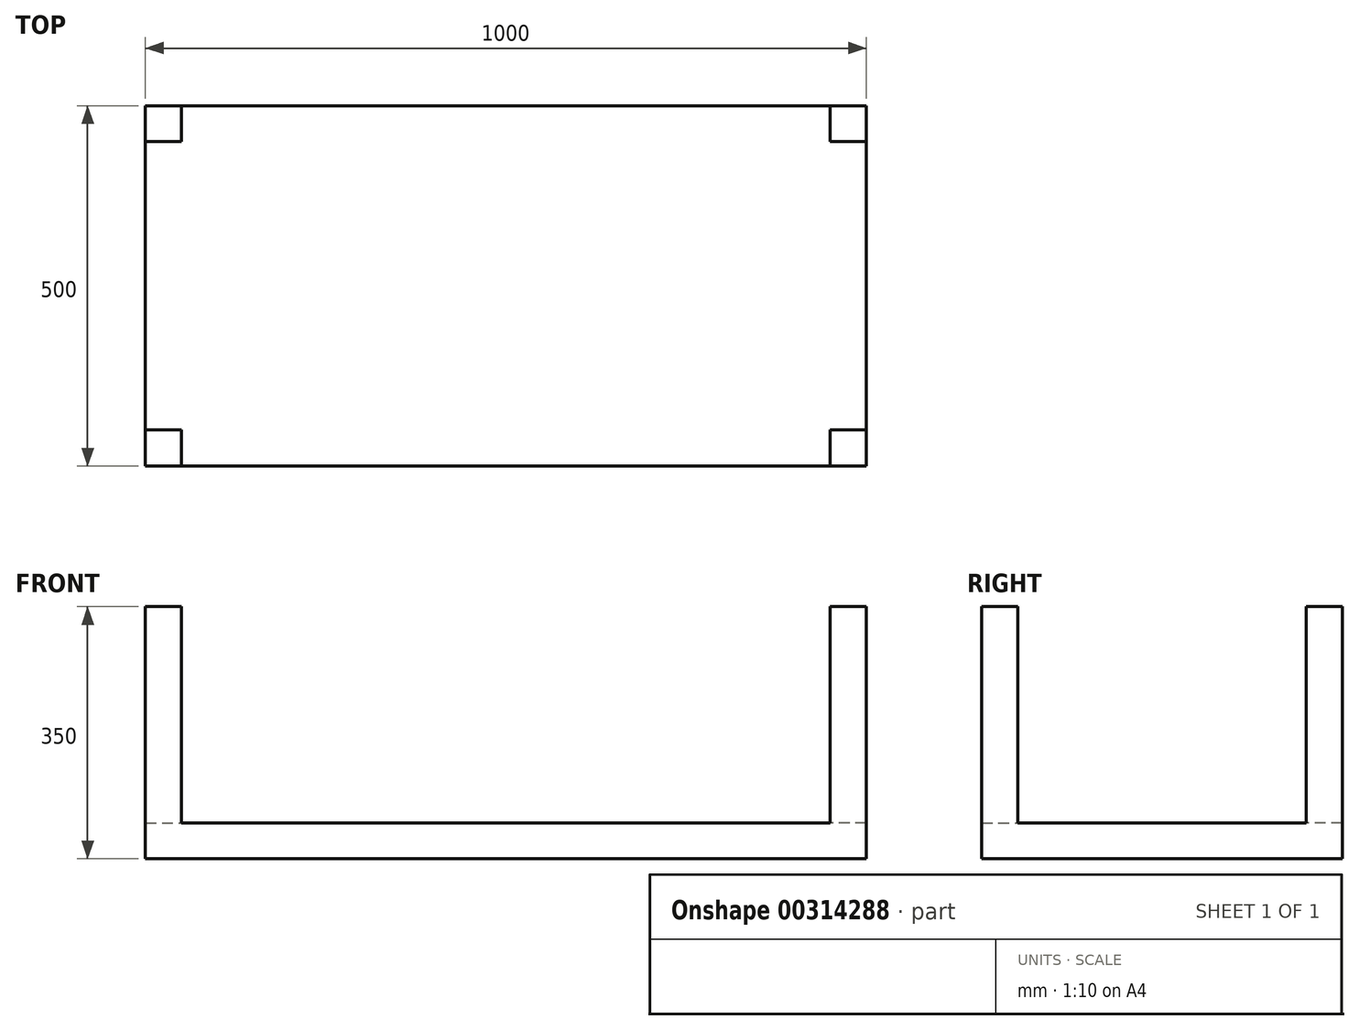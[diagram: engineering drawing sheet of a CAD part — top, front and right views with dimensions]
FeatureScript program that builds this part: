
annotation { "Feature Type Name" : "Feature", "Feature Type Description" : "" }
export const myFeature = defineFeature(function(context is Context, id is Id, definition is map)
    precondition{}
    {
        {
            var Q0;
            Q0=qCreatedBy(makeId("Top.planeOp"),FACE);
            var sketch = newSketch(context, id + "F0", { "sketchPlane" : qUnion([Q0])});
            skLineSegment(sketch, "E0.bottom", {"start": v(-382.04, 267.62) * mm, "end": v(617.96, 267.62) * mm});
            skLineSegment(sketch, "E0.top", {"start": v(-382.04, -232.38) * mm, "end": v(617.96, -232.38) * mm});
            skLineSegment(sketch, "E0.left", {"start": v(-382.04, 267.62) * mm, "end": v(-382.04, -232.38) * mm});
            skLineSegment(sketch, "E0.right", {"start": v(617.96, 267.62) * mm, "end": v(617.96, -232.38) * mm});
            skSolve(sketch);
        }
        {
            var Q0;
            Q0 = qSketchRegion(id + "F0", true);
            extrude(context, id + "F1", {"entities" : qUnion([Q0]), "depth" : 50 * mm});
        }
        {
            var Q0;
            Q0=makeQuery(id+"F1.opExtrude","CAP_FACE",FACE,{"disambiguationData":[OSD([sQuery(id+"F0.wireOp",EDGE,"E0.bottom"),sQuery(id+"F0.wireOp",EDGE,"E0.top"),sQuery(id+"F0.wireOp",EDGE,"E0.left"),sQuery(id+"F0.wireOp",EDGE,"E0.right")])],"isStart":false});
            var sketch = newSketch(context, id + "F2", { "sketchPlane" : qUnion([Q0])});
            skLineSegment(sketch, "E1.bottom", {"start": v(-382.04, 267.62) * mm, "end": v(-332.04, 267.62) * mm});
            skLineSegment(sketch, "E1.top", {"start": v(-382.04, 217.62) * mm, "end": v(-332.04, 217.62) * mm});
            skLineSegment(sketch, "E1.left", {"start": v(-382.04, 267.62) * mm, "end": v(-382.04, 217.62) * mm});
            skLineSegment(sketch, "E1.right", {"start": v(-332.04, 267.62) * mm, "end": v(-332.04, 217.62) * mm});
            skLineSegment(sketch, "E2.bottom", {"start": v(617.96, 267.62) * mm, "end": v(567.96, 267.62) * mm});
            skLineSegment(sketch, "E2.top", {"start": v(617.96, 217.62) * mm, "end": v(567.96, 217.62) * mm});
            skLineSegment(sketch, "E2.left", {"start": v(617.96, 267.62) * mm, "end": v(617.96, 217.62) * mm});
            skLineSegment(sketch, "E2.right", {"start": v(567.96, 267.62) * mm, "end": v(567.96, 217.62) * mm});
            skLineSegment(sketch, "E3.bottom", {"start": v(-382.04, -232.38) * mm, "end": v(-332.04, -232.38) * mm});
            skLineSegment(sketch, "E3.top", {"start": v(-382.04, -182.38) * mm, "end": v(-332.04, -182.38) * mm});
            skLineSegment(sketch, "E3.left", {"start": v(-382.04, -232.38) * mm, "end": v(-382.04, -182.38) * mm});
            skLineSegment(sketch, "E3.right", {"start": v(-332.04, -232.38) * mm, "end": v(-332.04, -182.38) * mm});
            skLineSegment(sketch, "E4.bottom", {"start": v(617.96, -232.38) * mm, "end": v(567.96, -232.38) * mm});
            skLineSegment(sketch, "E4.top", {"start": v(617.96, -182.38) * mm, "end": v(567.96, -182.38) * mm});
            skLineSegment(sketch, "E4.left", {"start": v(617.96, -232.38) * mm, "end": v(617.96, -182.38) * mm});
            skLineSegment(sketch, "E4.right", {"start": v(567.96, -232.38) * mm, "end": v(567.96, -182.38) * mm});
            skSolve(sketch);
        }
        {
            var Q0;
            Q0=makeQuery(id+"F2.imprint","IMPRINT",FACE,{"disambiguationData":[TD([[makeQuery(id+"F2.imprint","IMPRINT",EDGE,{"derivedFrom":sQuery(id+"F2.wireOp",EDGE,"E1.bottom")}),-1.0]])]});
            var Q1;
            Q1=makeQuery(id+"F2.imprint","IMPRINT",FACE,{"disambiguationData":[TD([[makeQuery(id+"F2.imprint","IMPRINT",EDGE,{"derivedFrom":sQuery(id+"F2.wireOp",EDGE,"E2.bottom")}),-1.0]])]});
            var Q2;
            Q2=makeQuery(id+"F2.imprint","IMPRINT",FACE,{"disambiguationData":[TD([[makeQuery(id+"F2.imprint","IMPRINT",EDGE,{"derivedFrom":sQuery(id+"F2.wireOp",EDGE,"E3.bottom")}),1.0]])]});
            var Q3;
            Q3=makeQuery(id+"F2.imprint","IMPRINT",FACE,{"disambiguationData":[TD([[makeQuery(id+"F2.imprint","IMPRINT",EDGE,{"derivedFrom":sQuery(id+"F2.wireOp",EDGE,"E4.bottom")}),1.0]])]});
            extrude(context, id + "F3", {"entities" : qUnion([Q0, Q1, Q2, Q3]), "operationType" : NewBodyOperationType.ADD, "depth" : 300 * mm});
        }
    });
